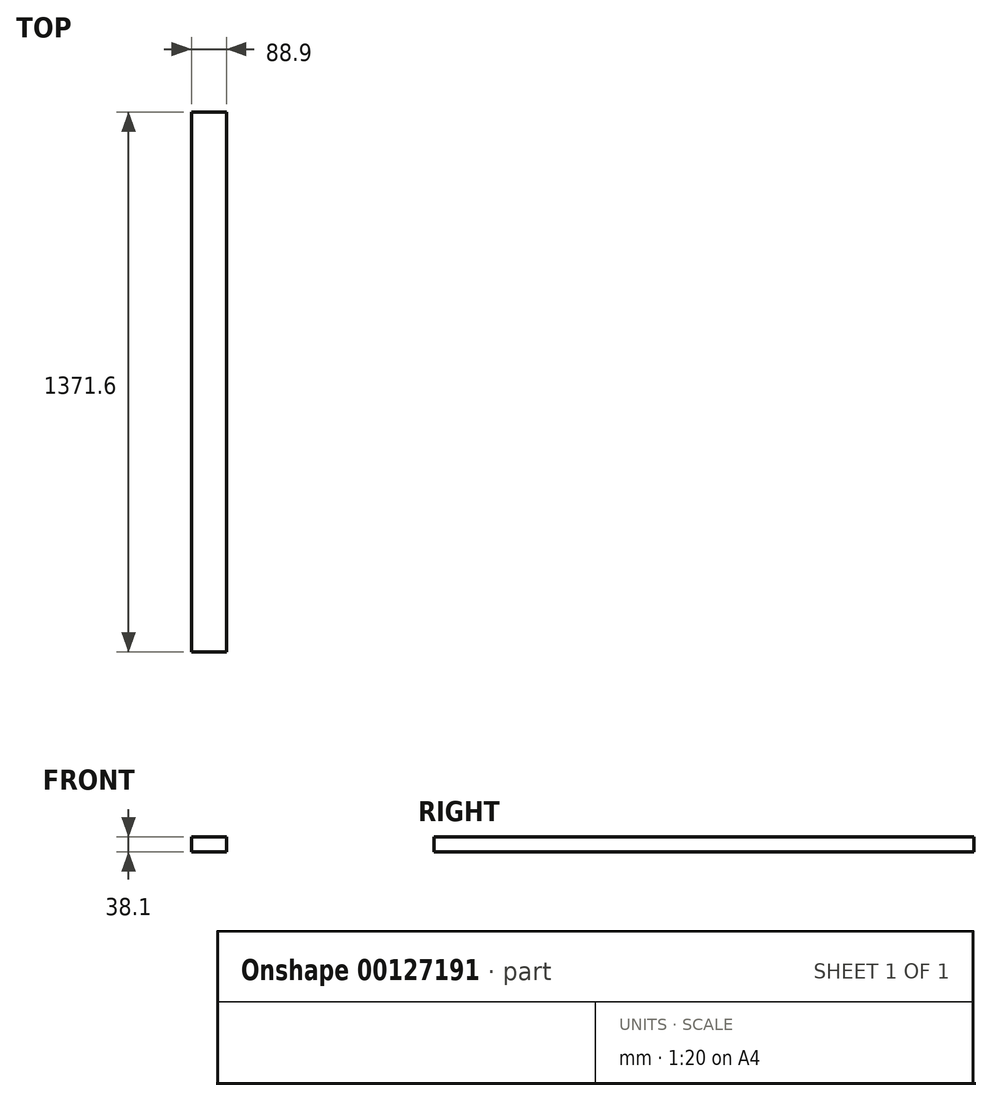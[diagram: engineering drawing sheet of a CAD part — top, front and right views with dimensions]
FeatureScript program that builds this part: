
annotation { "Feature Type Name" : "Feature", "Feature Type Description" : "" }
export const myFeature = defineFeature(function(context is Context, id is Id, definition is map)
    precondition{}
    {
        {
            var Q0;
            Q0=qCreatedBy(makeId("Front.planeOp"),FACE);
            var sketch = newSketch(context, id + "F0", { "sketchPlane" : qUnion([Q0])});
            skLineSegment(sketch, "E0.bottom", {"start": v(44.45, -19.05) * mm, "end": v(-44.45, -19.05) * mm});
            skLineSegment(sketch, "E0.top", {"start": v(44.45, 19.05) * mm, "end": v(-44.45, 19.05) * mm});
            skLineSegment(sketch, "E0.left", {"start": v(44.45, -19.05) * mm, "end": v(44.45, 19.05) * mm});
            skLineSegment(sketch, "E0.right", {"start": v(-44.45, -19.05) * mm, "end": v(-44.45, 19.05) * mm});
            skPoint(sketch, "E0.middle", {"position": v(0, 0) * mm});
            skSolve(sketch);
        }
        {
            var Q0;
            Q0=qSketchRegion(id+"F0",true);
            extrude(context, id + "F1", {"entities" : qUnion([Q0]), "depth" : 1371.6 * mm, "offsetDistance" : 25.4 * mm});
        }
    });
